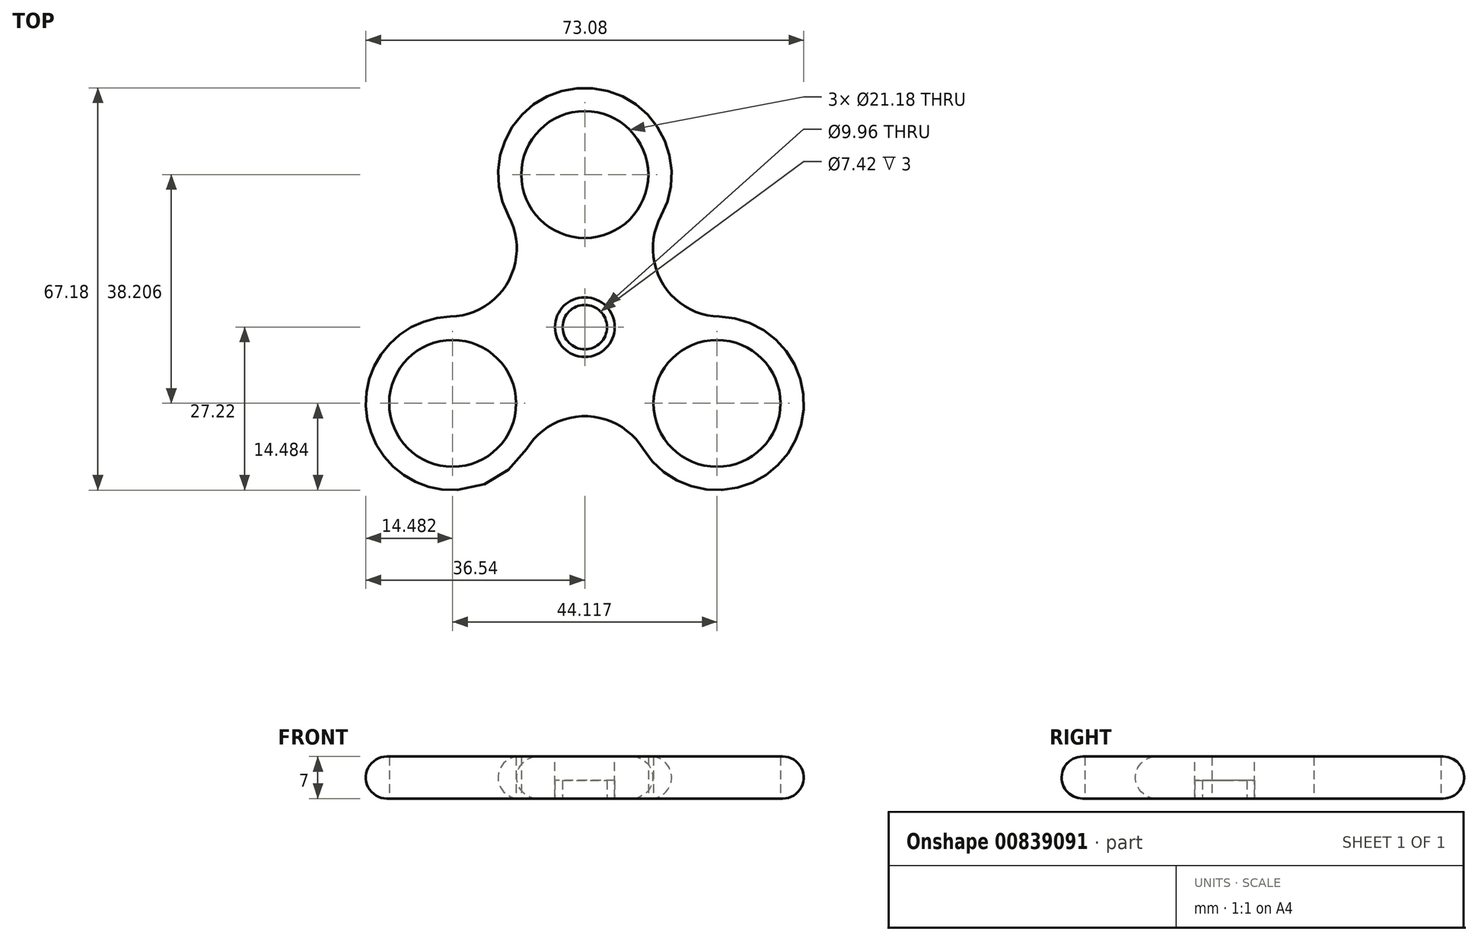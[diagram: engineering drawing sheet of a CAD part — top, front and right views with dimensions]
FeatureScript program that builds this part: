
annotation { "Feature Type Name" : "Feature", "Feature Type Description" : "" }
export const myFeature = defineFeature(function(context is Context, id is Id, definition is map)
    precondition{}
    {
        {
            var Q0;
            Q0=qCreatedBy(makeId("Top.planeOp"),FACE);
            var sketch = newSketch(context, id + "F0", { "sketchPlane" : qUnion([Q0])});
            skCircle(sketch, "E0", {"center": v(0, 0) * mm, "radius": 10.99 * mm});
            skCircle(sketch, "E1", {"center": v(0, 0) * mm, "radius": 25.47 * mm, "construction": true});
            skCircle(sketch, "E2", {"center": v(0, 25.47) * mm, "radius": 10.99 * mm});
            skCircle(sketch, "E3", {"center": v(-22.06, -12.74) * mm, "radius": 10.99 * mm});
            skCircle(sketch, "E4", {"center": v(22.06, -12.74) * mm, "radius": 10.99 * mm});
            skLineSegment(sketch, "E5", {"start": v(-22.06, -12.74) * mm, "end": v(22.06, -12.74) * mm, "construction": true});
            skLineSegment(sketch, "E6", {"start": v(0, 25.47) * mm, "end": v(-22.06, -12.74) * mm, "construction": true});
            skLineSegment(sketch, "E7", {"start": v(22.06, -12.74) * mm, "end": v(0, 25.47) * mm, "construction": true});
            skLineSegment(sketch, "E8.bottom", {"start": v(-57.15, 57.15) * mm, "end": v(57.15, 57.15) * mm, "construction": true});
            skLineSegment(sketch, "E8.top", {"start": v(-57.15, -57.15) * mm, "end": v(57.15, -57.15) * mm, "construction": true});
            skLineSegment(sketch, "E8.left", {"start": v(-57.15, 57.15) * mm, "end": v(-57.15, -57.15) * mm, "construction": true});
            skLineSegment(sketch, "E8.right", {"start": v(57.15, 57.15) * mm, "end": v(57.15, -57.15) * mm, "construction": true});
            skPoint(sketch, "E9", {"position": v(-57.15, 0) * mm});
            skPoint(sketch, "E10", {"position": v(0, 57.15) * mm});
            skSolve(sketch);
        }
        {
            var Q0;
            Q0=qCreatedBy(makeId("Top.planeOp"),FACE);
            var sketch = newSketch(context, id + "F1", { "sketchPlane" : qUnion([Q0])});
            skCircle(sketch, "E11", {"center": v(0, 0) * mm, "radius": 10.99 * mm});
            skCircle(sketch, "E12", {"center": v(-22.06, -12.74) * mm, "radius": 10.6 * mm});
            skCircle(sketch, "E13", {"center": v(0, 25.47) * mm, "radius": 10.6 * mm});
            skCircle(sketch, "E14", {"center": v(22.06, -12.74) * mm, "radius": 10.6 * mm});
            skLineSegment(sketch, "E15.bottom", {"start": v(-57.15, 57.15) * mm, "end": v(57.15, 57.15) * mm, "construction": true});
            skLineSegment(sketch, "E15.top", {"start": v(-57.15, -57.15) * mm, "end": v(57.15, -57.15) * mm, "construction": true});
            skLineSegment(sketch, "E15.left", {"start": v(-57.15, 57.15) * mm, "end": v(-57.15, -57.15) * mm, "construction": true});
            skLineSegment(sketch, "E15.right", {"start": v(57.15, 57.15) * mm, "end": v(57.15, -57.15) * mm, "construction": true});
            skPoint(sketch, "E16", {"position": v(-57.15, 0) * mm});
            skPoint(sketch, "E17", {"position": v(0, 57.15) * mm});
            skArc(sketch, "E18", {"start": v(-22.45, 1.74) * mm, "mid": v(-34.6, -19.98) * mm, "end": v(-9.71, -20.31) * mm});
            skArc(sketch, "E19", {"start": v(12.74, 18.57) * mm, "mid": v(0, 39.96) * mm, "end": v(-12.74, 18.57) * mm});
            skArc(sketch, "E20", {"start": v(9.71, -20.31) * mm, "mid": v(34.6, -19.98) * mm, "end": v(22.45, 1.74) * mm});
            skArc(sketch, "E21", {"start": v(-22.45, 1.74) * mm, "mid": v(-12.89, 7.44) * mm, "end": v(-12.74, 18.57) * mm});
            skArc(sketch, "E22", {"start": v(12.74, 18.57) * mm, "mid": v(12.89, 7.44) * mm, "end": v(22.45, 1.74) * mm});
            skArc(sketch, "E23", {"start": v(9.71, -20.31) * mm, "mid": v(0, -14.88) * mm, "end": v(-9.71, -20.31) * mm});
            skCircle(sketch, "E24", {"center": v(0, 0) * mm, "radius": 14.88 * mm, "construction": true});
            skSolve(sketch);
        }
        {
            var Q0;
            Q0 = qSketchRegion(id + "F1", true);
            extrude(context, id + "F2", {"entities" : qUnion([Q0]), "depth" : 7 * mm, "offsetDistance" : 25.4 * mm});
        }
        {
            var Q0;
            Q0=makeQuery(id+"F2.opExtrude","CAP_EDGE",EDGE,{"disambiguationData":[OSD([sQuery(id+"F1.wireOp",EDGE,"E18")])],"isStart":false});
            var Q1;
            Q1=makeQuery(id+"F2.opExtrude","CAP_EDGE",EDGE,{"disambiguationData":[OSD([sQuery(id+"F1.wireOp",EDGE,"E18")])],"isStart":true});
            fillet(context, id + "F3", {"entities" : qUnion([Q0, Q1]), "radius" : 3.5 * mm, "tangentPropagation" : true, "allowEdgeOverflow" : false});
        }
        {
            var Q0;
            Q0=makeQuery(id+"F2.opExtrude","CAP_FACE",FACE,{"disambiguationData":[OSD([sQuery(id+"F1.wireOp",EDGE,"E11"),sQuery(id+"F1.wireOp",EDGE,"E12"),sQuery(id+"F1.wireOp",EDGE,"E13"),sQuery(id+"F1.wireOp",EDGE,"E14"),sQuery(id+"F1.wireOp",EDGE,"E18"),sQuery(id+"F1.wireOp",EDGE,"E19"),sQuery(id+"F1.wireOp",EDGE,"E20"),sQuery(id+"F1.wireOp",EDGE,"E21"),sQuery(id+"F1.wireOp",EDGE,"E22"),sQuery(id+"F1.wireOp",EDGE,"E23")])],"isStart":false});
            var sketch = newSketch(context, id + "F4", { "sketchPlane" : qUnion([Q0])});
            skCircle(sketch, "E25", {"center": v(0, 0) * mm, "radius": 4.98 * mm});
            skCircle(sketch, "E26", {"center": v(0, 0) * mm, "radius": 10.99 * mm});
            skSolve(sketch);
        }
        {
            var Q0;
            Q0 = qSketchRegion(id + "F4", true);
            var Q1;
            Q1=makeQuery(id+"F2.opExtrude","CAP_FACE",FACE,{"disambiguationData":[OSD([sQuery(id+"F1.wireOp",EDGE,"E11"),sQuery(id+"F1.wireOp",EDGE,"E12"),sQuery(id+"F1.wireOp",EDGE,"E13"),sQuery(id+"F1.wireOp",EDGE,"E14"),sQuery(id+"F1.wireOp",EDGE,"E18"),sQuery(id+"F1.wireOp",EDGE,"E19"),sQuery(id+"F1.wireOp",EDGE,"E20"),sQuery(id+"F1.wireOp",EDGE,"E21"),sQuery(id+"F1.wireOp",EDGE,"E22"),sQuery(id+"F1.wireOp",EDGE,"E23")])],"isStart":true});
            var Q2;
            Q2=makeQuery(id+"F2.opExtrude","SWEPT_BODY",BODY,{"disambiguationData":[OSD([sQuery(id+"F1.wireOp",EDGE,"E11"),sQuery(id+"F1.wireOp",EDGE,"E12"),sQuery(id+"F1.wireOp",EDGE,"E13"),sQuery(id+"F1.wireOp",EDGE,"E14"),sQuery(id+"F1.wireOp",EDGE,"E18"),sQuery(id+"F1.wireOp",EDGE,"E19"),sQuery(id+"F1.wireOp",EDGE,"E20"),sQuery(id+"F1.wireOp",EDGE,"E21"),sQuery(id+"F1.wireOp",EDGE,"E22"),sQuery(id+"F1.wireOp",EDGE,"E23")])]});
            extrude(context, id + "F5", {"entities" : qUnion([Q0]), "operationType" : NewBodyOperationType.ADD, "endBound" : BoundingType.UP_TO_SURFACE, "oppositeDirection" : true, "depth" : 25.4 * mm, "endBoundEntityFace" : qUnion([Q1]), "endBoundEntityBody" : qUnion([Q2]), "offsetDistance" : 25.4 * mm});
        }
        {
            var Q0;
            {var subQ0=sQuery(id+"F1.wireOp",EDGE,"E23");var subQ1=sQuery(id+"F1.wireOp",EDGE,"E22");var subQ2=sQuery(id+"F1.wireOp",EDGE,"E21");var subQ3=sQuery(id+"F1.wireOp",EDGE,"E20");var subQ4=sQuery(id+"F1.wireOp",EDGE,"E19");var subQ5=sQuery(id+"F1.wireOp",EDGE,"E18");var subQ6=sQuery(id+"F1.wireOp",EDGE,"E14");var subQ7=sQuery(id+"F1.wireOp",EDGE,"E13");var subQ8=sQuery(id+"F1.wireOp",EDGE,"E12");var subQ9=sQuery(id+"F1.wireOp",EDGE,"E11");Q0=makeQuery(id+"F5.boolean.opBoolean","MERGE",FACE,{"derivedFrom":[makeQuery(id+"F2.opExtrude","CAP_FACE",FACE,{"disambiguationData":[OSD([subQ9,subQ8,subQ7,subQ6,subQ5,subQ4,subQ3,subQ2,subQ1,subQ0])],"isStart":true}),makeQuery(id+"F5.opExtrude","CAP_FACE",FACE,{"disambiguationData":[OSD([subQ9,subQ8,subQ7,subQ6,subQ5,subQ4,subQ3,subQ2,subQ1,subQ0])],"isStart":false})]});}
            var sketch = newSketch(context, id + "F6", { "sketchPlane" : qUnion([Q0])});
            skCircle(sketch, "E27", {"center": v(0, 0) * mm, "radius": 3.7 * mm});
            skCircle(sketch, "E28", {"center": v(0, 0) * mm, "radius": 4.98 * mm});
            skSolve(sketch);
        }
        {
            var Q0;
            Q0 = qSketchRegion(id + "F6", true);
            extrude(context, id + "F7", {"entities" : qUnion([Q0]), "oppositeDirection" : true, "depth" : 3 * mm, "offsetDistance" : 25.4 * mm});
        }
    });
